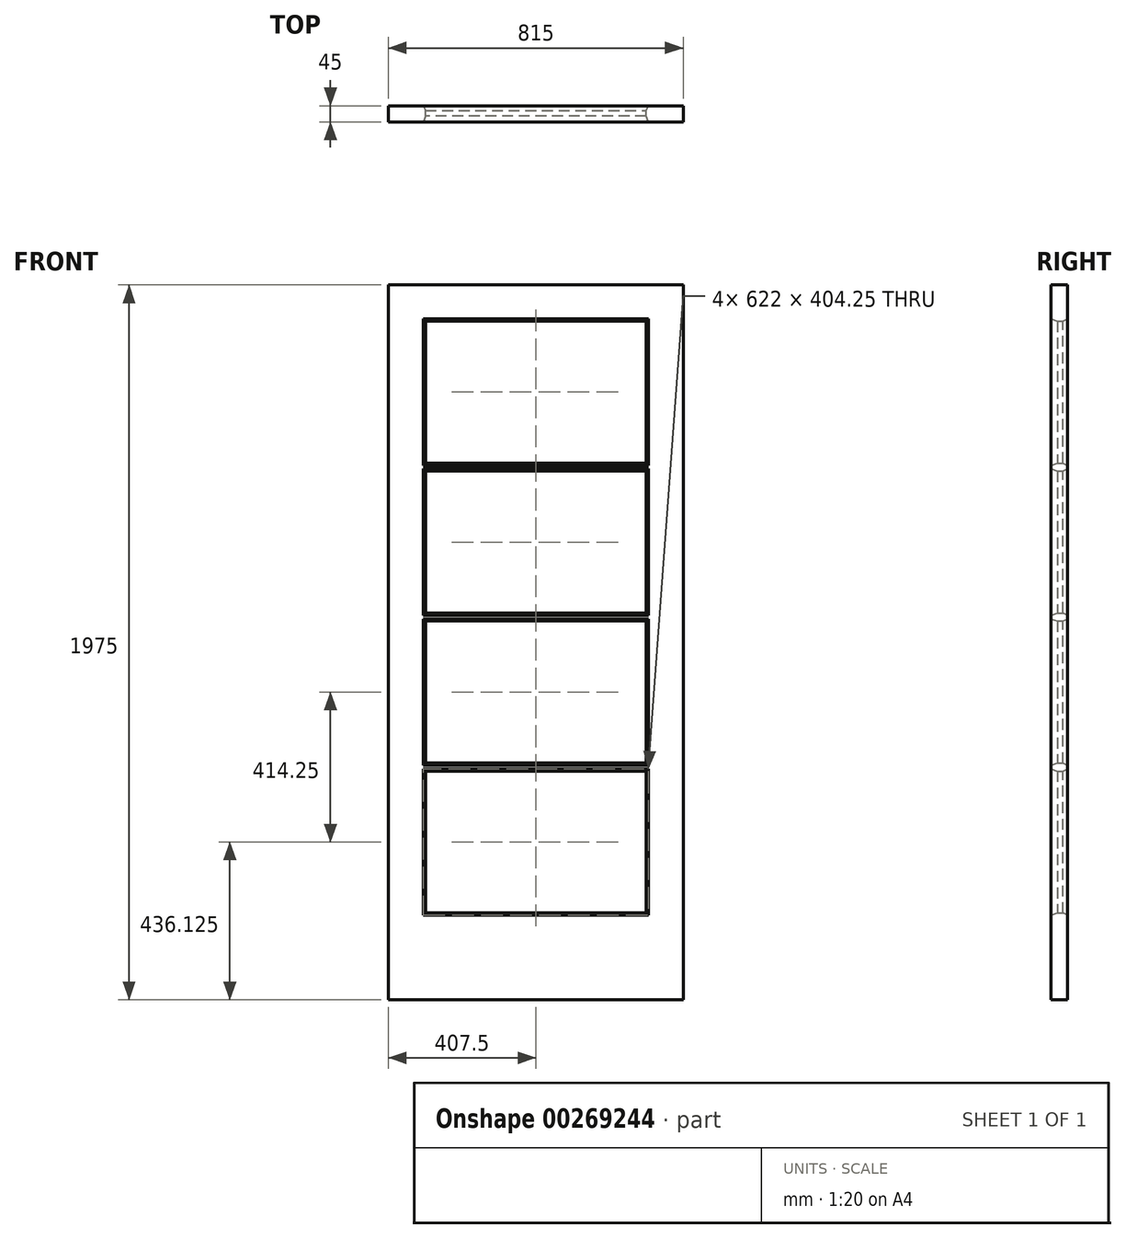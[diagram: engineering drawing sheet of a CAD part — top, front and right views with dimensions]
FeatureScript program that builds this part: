
annotation { "Feature Type Name" : "Feature", "Feature Type Description" : "" }
export const myFeature = defineFeature(function(context is Context, id is Id, definition is map)
    precondition{}
    {
        {
            var Q0;
            Q0=qCreatedBy(makeId("Front.planeOp"),FACE);
            var sketch = newSketch(context, id + "F0", { "sketchPlane" : qUnion([Q0])});
            skLineSegment(sketch, "E0.bottom", {"start": v(-407.5, 987.5) * mm, "end": v(407.5, 987.5) * mm});
            skLineSegment(sketch, "E0.top", {"start": v(-407.5, -987.5) * mm, "end": v(407.5, -987.5) * mm});
            skLineSegment(sketch, "E0.left", {"start": v(-407.5, 987.5) * mm, "end": v(-407.5, -987.5) * mm});
            skLineSegment(sketch, "E0.right", {"start": v(407.5, 987.5) * mm, "end": v(407.5, -987.5) * mm});
            skPoint(sketch, "E0.middle", {"position": v(0, 0) * mm});
            skLineSegment(sketch, "E1.bottom", {"start": v(-305, 887.5) * mm, "end": v(305, 887.5) * mm});
            skLineSegment(sketch, "E1.top", {"start": v(-305, 495.25) * mm, "end": v(305, 495.25) * mm});
            skLineSegment(sketch, "E1.left", {"start": v(-305, 887.5) * mm, "end": v(-305, 495.25) * mm});
            skLineSegment(sketch, "E1.right", {"start": v(305, 887.5) * mm, "end": v(305, 495.25) * mm});
            skLineSegment(sketch, "E2.bottom", {"start": v(-305, 473.25) * mm, "end": v(305, 473.25) * mm});
            skLineSegment(sketch, "E2.top", {"start": v(-305, 81) * mm, "end": v(305, 81) * mm});
            skLineSegment(sketch, "E2.left", {"start": v(-305, 473.25) * mm, "end": v(-305, 81) * mm});
            skLineSegment(sketch, "E2.right", {"start": v(305, 473.25) * mm, "end": v(305, 81) * mm});
            skLineSegment(sketch, "E3.bottom", {"start": v(-305, 59) * mm, "end": v(305, 59) * mm});
            skLineSegment(sketch, "E3.top", {"start": v(-305, -333.25) * mm, "end": v(305, -333.25) * mm});
            skLineSegment(sketch, "E3.left", {"start": v(-305, 59) * mm, "end": v(-305, -333.25) * mm});
            skLineSegment(sketch, "E3.right", {"start": v(305, 59) * mm, "end": v(305, -333.25) * mm});
            skLineSegment(sketch, "E4.bottom", {"start": v(-305, -355.25) * mm, "end": v(305, -355.25) * mm});
            skLineSegment(sketch, "E4.top", {"start": v(-305, -747.5) * mm, "end": v(305, -747.5) * mm});
            skLineSegment(sketch, "E4.left", {"start": v(-305, -355.25) * mm, "end": v(-305, -747.5) * mm});
            skLineSegment(sketch, "E4.right", {"start": v(305, -355.25) * mm, "end": v(305, -747.5) * mm});
            skLineSegment(sketch, "E5", {"start": v(-305, 495.25) * mm, "end": v(-305, 473.25) * mm, "construction": true});
            skLineSegment(sketch, "E6", {"start": v(-305, 81) * mm, "end": v(-305, 59) * mm, "construction": true});
            skLineSegment(sketch, "E7", {"start": v(-305, -333.25) * mm, "end": v(-305, -355.25) * mm, "construction": true});
            skSolve(sketch);
        }
        {
            var Q0;
            Q0=makeQuery(id+"F0.imprint","IMPRINT",FACE,{"disambiguationData":[TD([[makeQuery(id+"F0.imprint","IMPRINT",EDGE,{"derivedFrom":sQuery(id+"F0.wireOp",EDGE,"E0.bottom")}),-1.0]])]});
            extrude(context, id + "F1", {"entities" : qUnion([Q0]), "endBound" : BoundingType.SYMMETRIC, "depth" : 45 * mm});
        }
        {
            var Q0;
            Q0=makeQuery(id+"F1.opExtrude","CAP_EDGE",EDGE,{"disambiguationData":[OSD([sQuery(id+"F0.wireOp",EDGE,"E4.right")])],"isStart":false});
            var Q1;
            Q1=makeQuery(id+"F1.opExtrude","CAP_EDGE",EDGE,{"disambiguationData":[OSD([sQuery(id+"F0.wireOp",EDGE,"E4.bottom")])],"isStart":false});
            var Q2;
            Q2=makeQuery(id+"F1.opExtrude","CAP_EDGE",EDGE,{"disambiguationData":[OSD([sQuery(id+"F0.wireOp",EDGE,"E3.right")])],"isStart":false});
            var Q3;
            Q3=makeQuery(id+"F1.opExtrude","CAP_EDGE",EDGE,{"disambiguationData":[OSD([sQuery(id+"F0.wireOp",EDGE,"E3.bottom")])],"isStart":false});
            var Q4;
            Q4=makeQuery(id+"F1.opExtrude","CAP_EDGE",EDGE,{"disambiguationData":[OSD([sQuery(id+"F0.wireOp",EDGE,"E2.right")])],"isStart":false});
            var Q5;
            Q5=makeQuery(id+"F1.opExtrude","CAP_EDGE",EDGE,{"disambiguationData":[OSD([sQuery(id+"F0.wireOp",EDGE,"E2.bottom")])],"isStart":false});
            var Q6;
            Q6=makeQuery(id+"F1.opExtrude","CAP_EDGE",EDGE,{"disambiguationData":[OSD([sQuery(id+"F0.wireOp",EDGE,"E1.right")])],"isStart":false});
            var Q7;
            Q7=makeQuery(id+"F1.opExtrude","CAP_EDGE",EDGE,{"disambiguationData":[OSD([sQuery(id+"F0.wireOp",EDGE,"E1.bottom")])],"isStart":false});
            var Q8;
            Q8=makeQuery(id+"F1.opExtrude","CAP_EDGE",EDGE,{"disambiguationData":[OSD([sQuery(id+"F0.wireOp",EDGE,"E1.left")])],"isStart":false});
            var Q9;
            Q9=makeQuery(id+"F1.opExtrude","CAP_EDGE",EDGE,{"disambiguationData":[OSD([sQuery(id+"F0.wireOp",EDGE,"E1.top")])],"isStart":false});
            var Q10;
            Q10=makeQuery(id+"F1.opExtrude","CAP_EDGE",EDGE,{"disambiguationData":[OSD([sQuery(id+"F0.wireOp",EDGE,"E2.left")])],"isStart":false});
            var Q11;
            Q11=makeQuery(id+"F1.opExtrude","CAP_EDGE",EDGE,{"disambiguationData":[OSD([sQuery(id+"F0.wireOp",EDGE,"E2.top")])],"isStart":false});
            var Q12;
            Q12=makeQuery(id+"F1.opExtrude","CAP_EDGE",EDGE,{"disambiguationData":[OSD([sQuery(id+"F0.wireOp",EDGE,"E3.left")])],"isStart":false});
            var Q13;
            Q13=makeQuery(id+"F1.opExtrude","CAP_EDGE",EDGE,{"disambiguationData":[OSD([sQuery(id+"F0.wireOp",EDGE,"E3.top")])],"isStart":false});
            var Q14;
            Q14=makeQuery(id+"F1.opExtrude","CAP_EDGE",EDGE,{"disambiguationData":[OSD([sQuery(id+"F0.wireOp",EDGE,"E4.left")])],"isStart":false});
            var Q15;
            Q15=makeQuery(id+"F1.opExtrude","CAP_EDGE",EDGE,{"disambiguationData":[OSD([sQuery(id+"F0.wireOp",EDGE,"E4.top")])],"isStart":false});
            chamfer(context, id + "F2", {"entities" : qUnion([Q0, Q1, Q2, Q3, Q4, Q5, Q6, Q7, Q8, Q9, Q10, Q11, Q12, Q13, Q14, Q15]), "chamferType" : ChamferType.TWO_OFFSETS, "width1" : 6 * mm, "oppositeDirection" : false, "width2" : 17 * mm, "tangentPropagation" : true});
        }
        {
            var Q0;
            Q0=makeQuery(id+"F1.opExtrude","CAP_EDGE",EDGE,{"disambiguationData":[OSD([sQuery(id+"F0.wireOp",EDGE,"E4.top")])],"isStart":true});
            var Q1;
            Q1=makeQuery(id+"F1.opExtrude","CAP_EDGE",EDGE,{"disambiguationData":[OSD([sQuery(id+"F0.wireOp",EDGE,"E4.right")])],"isStart":true});
            var Q2;
            Q2=makeQuery(id+"F1.opExtrude","CAP_EDGE",EDGE,{"disambiguationData":[OSD([sQuery(id+"F0.wireOp",EDGE,"E4.bottom")])],"isStart":true});
            var Q3;
            Q3=makeQuery(id+"F1.opExtrude","CAP_EDGE",EDGE,{"disambiguationData":[OSD([sQuery(id+"F0.wireOp",EDGE,"E4.left")])],"isStart":true});
            var Q4;
            Q4=makeQuery(id+"F1.opExtrude","CAP_EDGE",EDGE,{"disambiguationData":[OSD([sQuery(id+"F0.wireOp",EDGE,"E3.left")])],"isStart":true});
            var Q5;
            Q5=makeQuery(id+"F1.opExtrude","CAP_EDGE",EDGE,{"disambiguationData":[OSD([sQuery(id+"F0.wireOp",EDGE,"E3.bottom")])],"isStart":true});
            var Q6;
            Q6=makeQuery(id+"F1.opExtrude","CAP_EDGE",EDGE,{"disambiguationData":[OSD([sQuery(id+"F0.wireOp",EDGE,"E2.left")])],"isStart":true});
            var Q7;
            Q7=makeQuery(id+"F1.opExtrude","CAP_EDGE",EDGE,{"disambiguationData":[OSD([sQuery(id+"F0.wireOp",EDGE,"E3.top")])],"isStart":true});
            var Q8;
            Q8=makeQuery(id+"F1.opExtrude","CAP_EDGE",EDGE,{"disambiguationData":[OSD([sQuery(id+"F0.wireOp",EDGE,"E3.right")])],"isStart":true});
            var Q9;
            Q9=makeQuery(id+"F1.opExtrude","CAP_EDGE",EDGE,{"disambiguationData":[OSD([sQuery(id+"F0.wireOp",EDGE,"E2.top")])],"isStart":true});
            var Q10;
            Q10=makeQuery(id+"F1.opExtrude","CAP_EDGE",EDGE,{"disambiguationData":[OSD([sQuery(id+"F0.wireOp",EDGE,"E2.right")])],"isStart":true});
            var Q11;
            Q11=makeQuery(id+"F1.opExtrude","CAP_EDGE",EDGE,{"disambiguationData":[OSD([sQuery(id+"F0.wireOp",EDGE,"E2.bottom")])],"isStart":true});
            var Q12;
            Q12=makeQuery(id+"F1.opExtrude","CAP_EDGE",EDGE,{"disambiguationData":[OSD([sQuery(id+"F0.wireOp",EDGE,"E1.right")])],"isStart":true});
            var Q13;
            Q13=makeQuery(id+"F1.opExtrude","CAP_EDGE",EDGE,{"disambiguationData":[OSD([sQuery(id+"F0.wireOp",EDGE,"E1.bottom")])],"isStart":true});
            var Q14;
            Q14=makeQuery(id+"F1.opExtrude","CAP_EDGE",EDGE,{"disambiguationData":[OSD([sQuery(id+"F0.wireOp",EDGE,"E1.left")])],"isStart":true});
            var Q15;
            Q15=makeQuery(id+"F1.opExtrude","CAP_EDGE",EDGE,{"disambiguationData":[OSD([sQuery(id+"F0.wireOp",EDGE,"E1.top")])],"isStart":true});
            chamfer(context, id + "F3", {"entities" : qUnion([Q0, Q1, Q2, Q3, Q4, Q5, Q6, Q7, Q8, Q9, Q10, Q11, Q12, Q13, Q14, Q15]), "chamferType" : ChamferType.TWO_OFFSETS, "width1" : 6 * mm, "oppositeDirection" : false, "width2" : 13 * mm, "tangentPropagation" : true});
        }
    });
